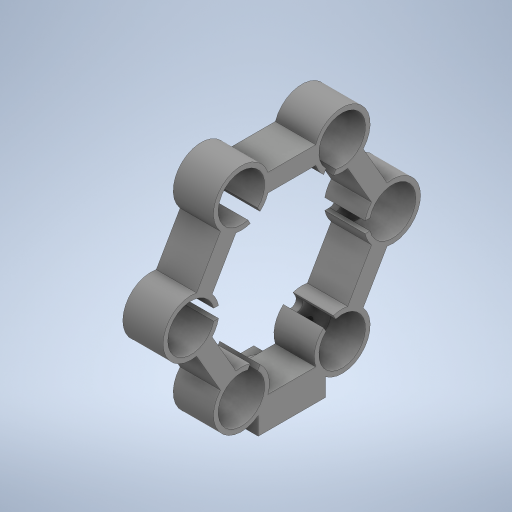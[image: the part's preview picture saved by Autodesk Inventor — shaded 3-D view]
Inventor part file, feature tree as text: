
AUTODESK INVENTOR PART (.ipt)
format: ipt  version: 2023 (Build 270158000, 158)  size: 477,696 bytes
history: native  units: in
note: dims shown in document units (in); Inventor stores cm internally (conversion verified against a paired STEP export)
features: extrude x6, sketch x3, projected_geometry x1
ambient origin geometry x8: Origin, YZ Plane, XZ Plane, XY Plane, X Axis, Y Axis, Z Axis, Center Point
bodies: Solid1 (feature_tree)
feature tree (10):
  sketch  "Sketch1"  dims[d0=1.378in d1=1.7717in]
  extrude  "Extrusion1"  Depth=1.7717in
  extrude  "Extrusion2"  Depth=0.8189in
  extrude  "Extrusion3"  Depth=0.315in
  extrude  "Extrusion4"  Depth=0.315in
  extrude  "Extrusion5"  Depth=0.1969in TaperAngle=360.0deg
  extrude  "Extrusion6"  Depth=0.1575in
  sketch  "Sketch2"  dims[d2=0.9843in d3=0.8189in]
  sketch  "Sketch3"  dims[d4=1.1811in d5=0.315in d6=0.315in d7=2.3622in d9=360.0deg d11=0.1575in d12=0.1575in d13=2.3622in d15=360.0deg d17=0.0984in d18=0.0984in d20=2.3622in d22=360.0deg d24=1.1811in d25=0.315in d26=1.1811in d28=1.378in d29=1.378in d30=0.1575in d31=0.7087in d32=0.0in d33=0.5906in d34=0.0in d35=0.1575in d36=2.3622in d38=360.0deg d40=0.7087in d41=0.0in d42=1.2598in d43=0.0in d44=0.1181in d45=0.1969in d46=0.0in d47=0.7874in d48=0.7874in d49=0.1181in d50=1.5748in d52=360.0deg d54=0.1969in d55=0.0in d56=0.0197in d57=0.0344in]
  projected_geometry  "Projected Loop1"
